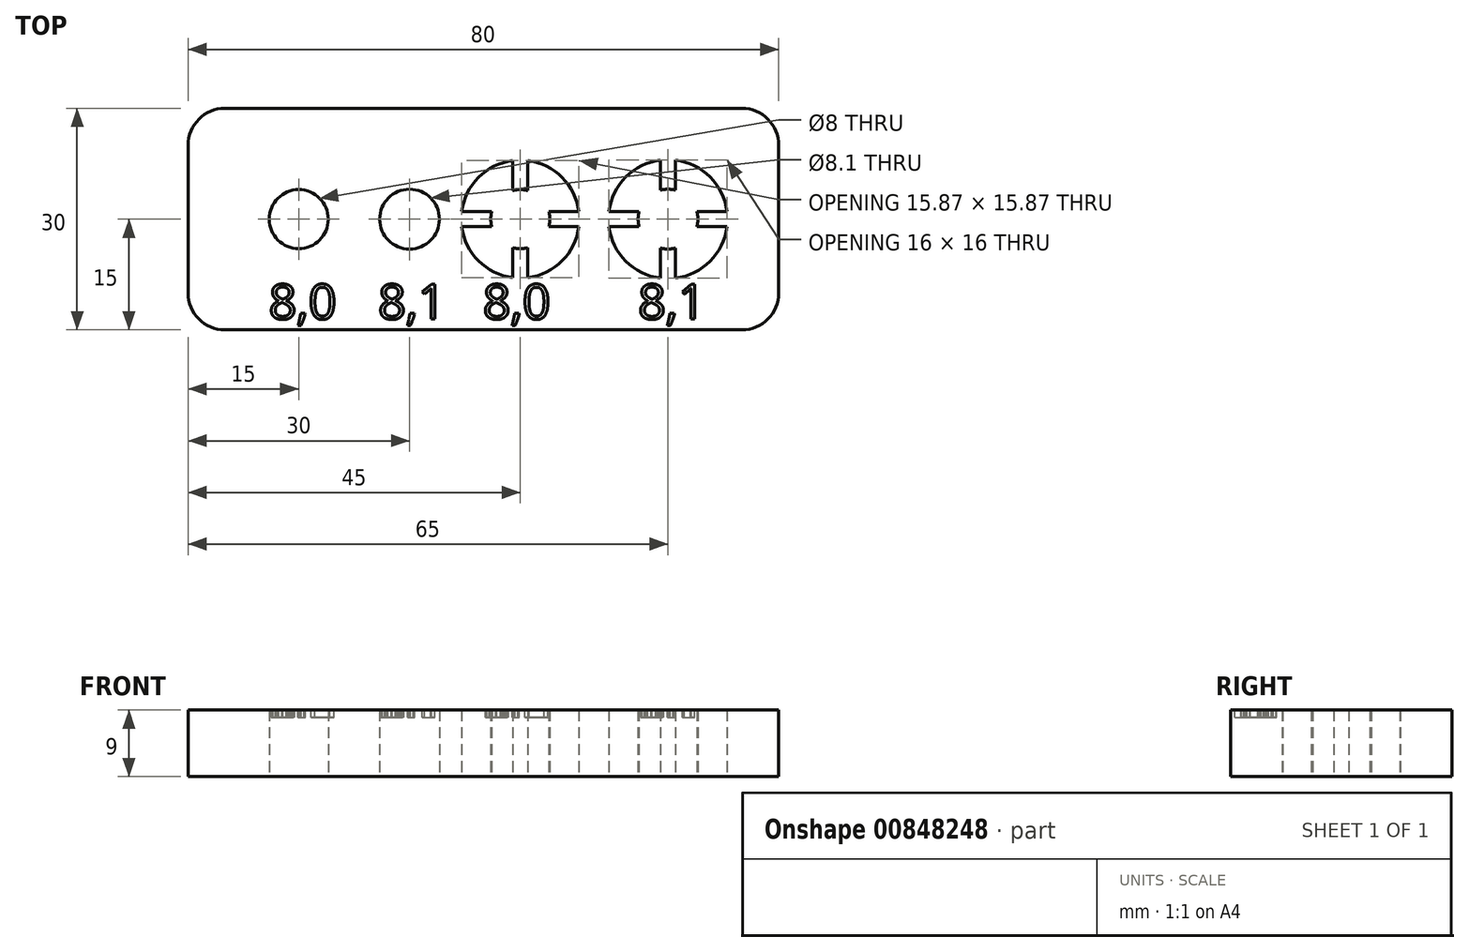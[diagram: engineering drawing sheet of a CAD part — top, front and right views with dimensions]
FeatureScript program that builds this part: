
annotation { "Feature Type Name" : "Feature", "Feature Type Description" : "" }
export const myFeature = defineFeature(function(context is Context, id is Id, definition is map)
    precondition{}
    {
        {
            var Q0;
            Q0=qCreatedBy(makeId("Top.planeOp"),FACE);
            var sketch = newSketch(context, id + "F0", { "sketchPlane" : qUnion([Q0])});
            skCircle(sketch, "E0", {"center": v(-25, 0) * mm, "radius": 4 * mm});
            skCircle(sketch, "E1", {"center": v(-10, 0) * mm, "radius": 4.05 * mm});
            skArc(sketch, "E2", {"start": v(6, 3.87) * mm, "mid": v(5, 4) * mm, "end": v(4, 3.87) * mm});
            skLineSegment(sketch, "E3.left", {"start": v(4, 7.94) * mm, "end": v(4, 3.87) * mm});
            skLineSegment(sketch, "E3.right", {"start": v(6, 7.94) * mm, "end": v(6, 3.87) * mm});
            skLineSegment(sketch, "E4.bottom", {"start": v(-2.94, 1) * mm, "end": v(1.13, 1) * mm});
            skLineSegment(sketch, "E4.top", {"start": v(-2.94, -1) * mm, "end": v(1.13, -1) * mm});
            skArc(sketch, "E5", {"start": v(12.94, 1) * mm, "mid": v(10.66, 5.66) * mm, "end": v(6, 7.94) * mm});
            skArc(sketch, "E6", {"start": v(26, 3.92) * mm, "mid": v(25, 4.05) * mm, "end": v(24, 3.92) * mm});
            skLineSegment(sketch, "E7.left", {"start": v(24, 8) * mm, "end": v(24, 3.92) * mm});
            skLineSegment(sketch, "E7.right", {"start": v(26, 8) * mm, "end": v(26, 3.92) * mm});
            skLineSegment(sketch, "E8.bottom", {"start": v(17, 1) * mm, "end": v(21.08, 1) * mm});
            skLineSegment(sketch, "E8.top", {"start": v(17, -1) * mm, "end": v(21.08, -1) * mm});
            skArc(sketch, "E9", {"start": v(26, -8) * mm, "mid": v(30.7, -5.7) * mm, "end": v(33, -1) * mm});
            skLineSegment(sketch, "E10.trimOffspring", {"start": v(6, -3.87) * mm, "end": v(6, -7.94) * mm});
            skLineSegment(sketch, "E11.trimOffspring", {"start": v(8.87, 1) * mm, "end": v(12.94, 1) * mm});
            skLineSegment(sketch, "E12.trimOffspring", {"start": v(4, -3.87) * mm, "end": v(4, -7.94) * mm});
            skArc(sketch, "E13.trimOffspring", {"start": v(1.13, 1) * mm, "mid": v(1, 0) * mm, "end": v(1.13, -1) * mm});
            skLineSegment(sketch, "E14.trimOffspring", {"start": v(8.87, -1) * mm, "end": v(12.94, -1) * mm});
            skArc(sketch, "E15.trimOffspring", {"start": v(4, -3.87) * mm, "mid": v(5, -4) * mm, "end": v(6, -3.87) * mm});
            skArc(sketch, "E16.trimOffspring", {"start": v(8.87, -1) * mm, "mid": v(9, 0) * mm, "end": v(8.87, 1) * mm});
            skLineSegment(sketch, "E17.trimOffspring", {"start": v(28.92, 1) * mm, "end": v(33, 1) * mm});
            skLineSegment(sketch, "E18.trimOffspring", {"start": v(26, -3.92) * mm, "end": v(26, -8) * mm});
            skLineSegment(sketch, "E19.trimOffspring", {"start": v(24, -3.92) * mm, "end": v(24, -8) * mm});
            skLineSegment(sketch, "E20.trimOffspring", {"start": v(28.92, -1) * mm, "end": v(33, -1) * mm});
            skArc(sketch, "E21.trimOffspring", {"start": v(28.92, -1) * mm, "mid": v(29.05, 0) * mm, "end": v(28.92, 1) * mm});
            skArc(sketch, "E22.trimOffspring", {"start": v(24, -3.92) * mm, "mid": v(25, -4.05) * mm, "end": v(26, -3.92) * mm});
            skArc(sketch, "E23.trimOffspring", {"start": v(21.08, 1) * mm, "mid": v(20.95, 0) * mm, "end": v(21.08, -1) * mm});
            skArc(sketch, "E24.trimOffspring", {"start": v(-2.94, -1) * mm, "mid": v(-0.66, -5.66) * mm, "end": v(4, -7.94) * mm});
            skArc(sketch, "E25.trimOffspring", {"start": v(4, 7.94) * mm, "mid": v(-0.66, 5.66) * mm, "end": v(-2.94, 1) * mm});
            skArc(sketch, "E26.trimOffspring", {"start": v(6, -7.94) * mm, "mid": v(10.66, -5.66) * mm, "end": v(12.94, -1) * mm});
            skArc(sketch, "E27.trimOffspring", {"start": v(24, 8) * mm, "mid": v(19.3, 5.7) * mm, "end": v(17, 1) * mm});
            skArc(sketch, "E28.trimOffspring", {"start": v(33, 1) * mm, "mid": v(30.7, 5.7) * mm, "end": v(26, 8) * mm});
            skArc(sketch, "E29.trimOffspring", {"start": v(17, -1) * mm, "mid": v(19.3, -5.7) * mm, "end": v(24, -8) * mm});
            skLineSegment(sketch, "E30.bottom", {"start": v(-35, 15) * mm, "end": v(35, 15) * mm});
            skLineSegment(sketch, "E30.top", {"start": v(-35, -15) * mm, "end": v(35, -15) * mm});
            skLineSegment(sketch, "E30.left", {"start": v(-40, 10) * mm, "end": v(-40, -10) * mm});
            skLineSegment(sketch, "E30.right", {"start": v(40, 10) * mm, "end": v(40, -10) * mm});
            skPoint(sketch, "E30.middle", {"position": v(0, 0) * mm});
            skPoint(sketch, "E31.visualSharp", {"position": v(-40, 15) * mm});
            skArc(sketch, "E31.filletArc", {"start": v(-35, 15) * mm, "mid": v(-38.54, 13.54) * mm, "end": v(-40, 10) * mm});
            skPoint(sketch, "E32.visualSharp", {"position": v(-40, -15) * mm});
            skArc(sketch, "E32.filletArc", {"start": v(-40, -10) * mm, "mid": v(-38.54, -13.54) * mm, "end": v(-35, -15) * mm});
            skPoint(sketch, "E33.visualSharp", {"position": v(40, -15) * mm});
            skArc(sketch, "E33.filletArc", {"start": v(35, -15) * mm, "mid": v(38.54, -13.54) * mm, "end": v(40, -10) * mm});
            skPoint(sketch, "E34.visualSharp", {"position": v(40, 15) * mm});
            skArc(sketch, "E34.filletArc", {"start": v(40, 10) * mm, "mid": v(38.54, 13.54) * mm, "end": v(35, 15) * mm});
            skSolve(sketch);
        }
        {
            var Q0;
            Q0 = qSketchRegion(id + "F0", true);
            extrude(context, id + "F1", {"entities" : qUnion([Q0]), "depth" : 9 * mm, "offsetDistance" : 25 * mm});
        }
        {
            var Q0;
            Q0=makeQuery(id+"F1.opExtrude","CAP_FACE",FACE,{"disambiguationData":[OSD([sQuery(id+"F0.wireOp",EDGE,"E0"),sQuery(id+"F0.wireOp",EDGE,"E1"),sQuery(id+"F0.wireOp",EDGE,"E2"),sQuery(id+"F0.wireOp",EDGE,"E3.left"),sQuery(id+"F0.wireOp",EDGE,"E3.right"),sQuery(id+"F0.wireOp",EDGE,"E4.bottom"),sQuery(id+"F0.wireOp",EDGE,"E4.top"),sQuery(id+"F0.wireOp",EDGE,"E5"),sQuery(id+"F0.wireOp",EDGE,"E6"),sQuery(id+"F0.wireOp",EDGE,"E7.left"),sQuery(id+"F0.wireOp",EDGE,"E7.right"),sQuery(id+"F0.wireOp",EDGE,"E8.bottom"),sQuery(id+"F0.wireOp",EDGE,"E8.top"),sQuery(id+"F0.wireOp",EDGE,"E9"),sQuery(id+"F0.wireOp",EDGE,"E10.trimOffspring"),sQuery(id+"F0.wireOp",EDGE,"E11.trimOffspring"),sQuery(id+"F0.wireOp",EDGE,"E12.trimOffspring"),sQuery(id+"F0.wireOp",EDGE,"E13.trimOffspring"),sQuery(id+"F0.wireOp",EDGE,"E14.trimOffspring"),sQuery(id+"F0.wireOp",EDGE,"E15.trimOffspring"),sQuery(id+"F0.wireOp",EDGE,"E16.trimOffspring"),sQuery(id+"F0.wireOp",EDGE,"E17.trimOffspring"),sQuery(id+"F0.wireOp",EDGE,"E18.trimOffspring"),sQuery(id+"F0.wireOp",EDGE,"E19.trimOffspring"),sQuery(id+"F0.wireOp",EDGE,"E20.trimOffspring"),sQuery(id+"F0.wireOp",EDGE,"E21.trimOffspring"),sQuery(id+"F0.wireOp",EDGE,"E22.trimOffspring"),sQuery(id+"F0.wireOp",EDGE,"E23.trimOffspring"),sQuery(id+"F0.wireOp",EDGE,"E24.trimOffspring"),sQuery(id+"F0.wireOp",EDGE,"E25.trimOffspring"),sQuery(id+"F0.wireOp",EDGE,"E26.trimOffspring"),sQuery(id+"F0.wireOp",EDGE,"E27.trimOffspring"),sQuery(id+"F0.wireOp",EDGE,"E28.trimOffspring"),sQuery(id+"F0.wireOp",EDGE,"E29.trimOffspring"),sQuery(id+"F0.wireOp",EDGE,"E30.bottom"),sQuery(id+"F0.wireOp",EDGE,"E30.top"),sQuery(id+"F0.wireOp",EDGE,"E30.left"),sQuery(id+"F0.wireOp",EDGE,"E30.right"),sQuery(id+"F0.wireOp",EDGE,"E31.filletArc"),sQuery(id+"F0.wireOp",EDGE,"E32.filletArc"),sQuery(id+"F0.wireOp",EDGE,"E33.filletArc"),sQuery(id+"F0.wireOp",EDGE,"E34.filletArc")])],"isStart":false});
            var sketch = newSketch(context, id + "F2", { "sketchPlane" : qUnion([Q0])});
            skText(sketch, "E35", { "text": "8,0", "fontName": "OpenSans-Regular.ttf"});
            skText(sketch, "E36", { "text": "8,1", "fontName": "OpenSans-Regular.ttf"});
            skText(sketch, "E37", { "text": "8,0", "fontName": "OpenSans-Regular.ttf"});
            skText(sketch, "E38", { "text": "8,1", "fontName": "OpenSans-Regular.ttf"});
            const initialGuessF2  = {"E35": [-0.02905, -0.01354, 1, 0, 0.00474], "E36": [-0.01425, -0.01354, 1, 0, 0.00474], "E37": [-7e-05, -0.01354, 1, 0, 0.00474], "E38": [0.02095, -0.01354, 1, 0, 0.00474]};
            skSetInitialGuess(sketch, initialGuessF2);
            skSolve(sketch);
        }
        {
            var Q0;
            Q0 = qSketchRegion(id + "F2", true);
            extrude(context, id + "F3", {"entities" : qUnion([Q0]), "operationType" : NewBodyOperationType.REMOVE, "oppositeDirection" : true, "depth" : 1 * mm, "offsetDistance" : 25 * mm});
        }
    });
